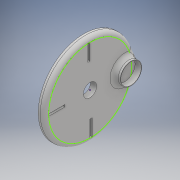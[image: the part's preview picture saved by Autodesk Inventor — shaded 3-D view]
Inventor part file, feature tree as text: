
AUTODESK INVENTOR PART (.ipt)
format: ipt  version: 2018 (Build 220112000, 112)  size: 215,040 bytes
history: native  units: mm
features: sketch x5, extrude x4, fillet x2
ambient origin geometry x8: Origin, YZ Plane, XZ Plane, XY Plane, X Axis, Y Axis, Z Axis, Center Point
bodies: Solid1 (feature_tree)
feature tree (11):
  extrude  "Extrusion1"  Depth=3.0mm TaperAngle=0.0deg
  extrude  "Extrusion2"  Depth=3.0mm TaperAngle=0.0deg
  fillet  "Fillet1"  Radius=2.0mm
  fillet  "Fillet2"  Radius=2.0mm
  extrude  "Extrusion3"  Depth=3.0mm TaperAngle=0.0deg
  sketch  "Sketch4"  dims[d11=8.0mm d12=1.0mm]
  extrude  "Extrusion4"  Depth=1.0mm
  sketch  "Sketch1"  dims[d0=44.45mm d1=3.0mm d2=0.0mm]
  sketch  "Sketch2"  dims[d3=10.0mm d4=3.0mm d5=0.0mm d6=2.0mm d7=2.0mm]
  sketch  "Sketch3"  dims[d8=6.5mm d9=3.0mm d10=0.0mm]
  sketch  "Sketch5"  dims[d13=1.0mm d14=8.0mm d15=8.0mm d16=1.0mm d17=2.0mm d18=0.0mm]
